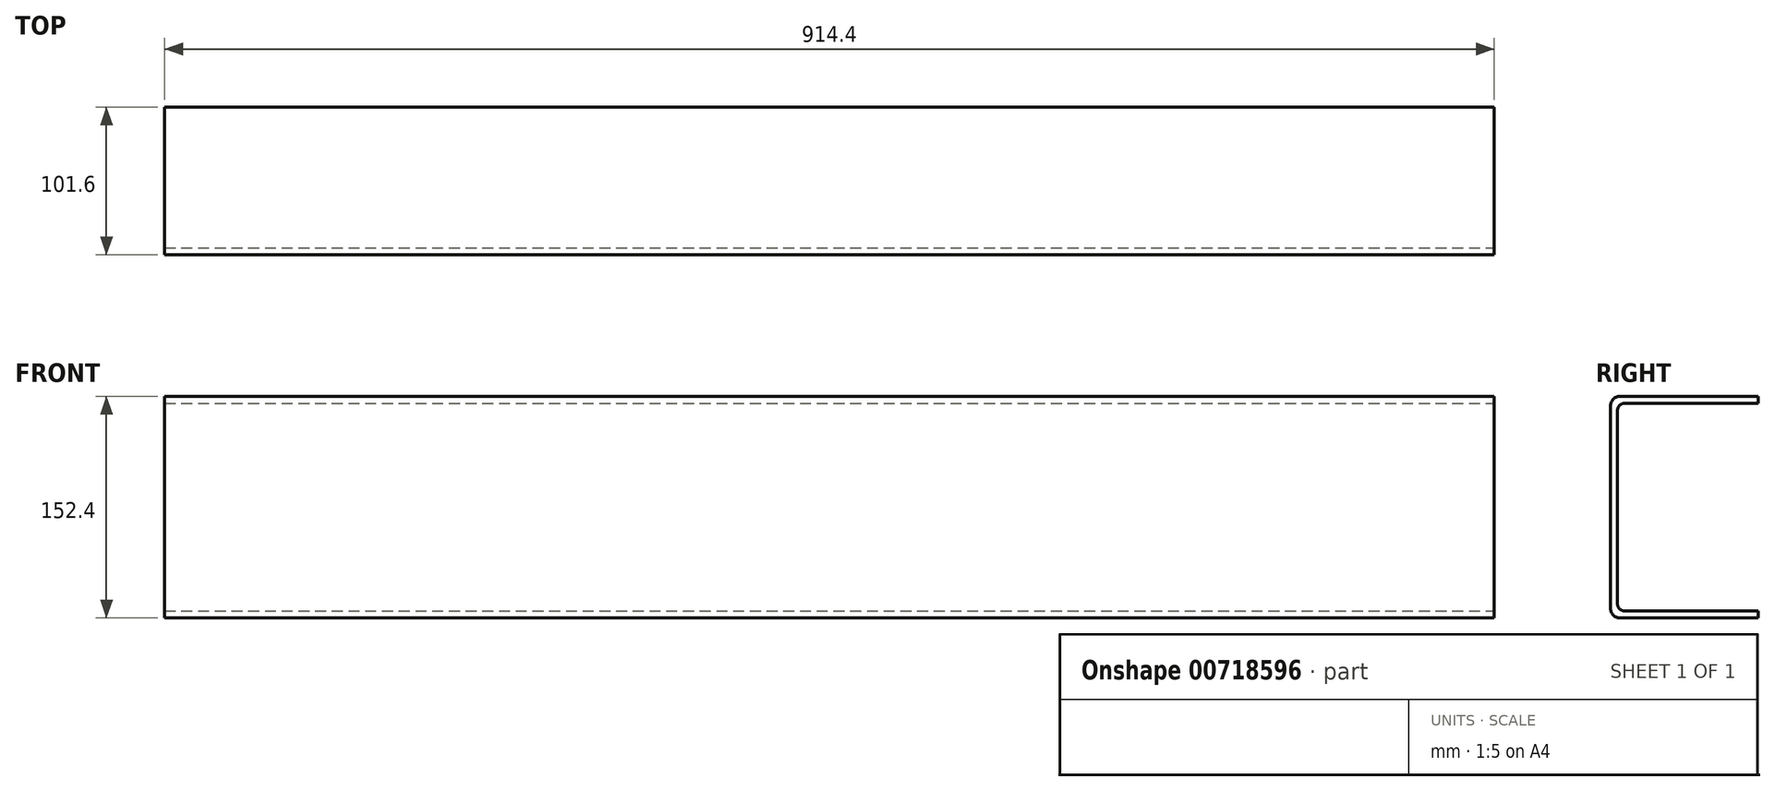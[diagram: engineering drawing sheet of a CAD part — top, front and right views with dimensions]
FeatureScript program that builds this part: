
annotation { "Feature Type Name" : "Feature", "Feature Type Description" : "" }
export const myFeature = defineFeature(function(context is Context, id is Id, definition is map)
    precondition{}
    {
        {
            var Q0;
            Q0=qCreatedBy(makeId("Right.planeOp"),FACE);
            var sketch = newSketch(context, id + "F0", { "sketchPlane" : qUnion([Q0])});
            skLineSegment(sketch, "E0", {"start": v(101.6, 76.2) * mm, "end": v(6.35, 76.2) * mm});
            skLineSegment(sketch, "E1", {"start": v(0, 69.85) * mm, "end": v(0, 0) * mm});
            skLineSegment(sketch, "E2", {"start": v(-101.6, 0) * mm, "end": v(84.67, 0) * mm, "construction": true});
            skLineSegment(sketch, "E3.MirrorCS", {"start": v(101.6, -76.2) * mm, "end": v(6.35, -76.2) * mm});
            skLineSegment(sketch, "E4.MirrorCS", {"start": v(0, -69.85) * mm, "end": v(0, 0) * mm});
            skLineSegment(sketch, "E5.0", {"start": v(101.6, -71.44) * mm, "end": v(9.53, -71.44) * mm});
            skLineSegment(sketch, "E5.1", {"start": v(4.76, -66.67) * mm, "end": v(4.76, 0) * mm});
            skLineSegment(sketch, "E5.2", {"start": v(4.76, 66.67) * mm, "end": v(4.76, 0) * mm});
            skLineSegment(sketch, "E5.3", {"start": v(101.6, 71.44) * mm, "end": v(9.52, 71.44) * mm});
            skLineSegment(sketch, "E6", {"start": v(101.6, 76.2) * mm, "end": v(101.6, 71.44) * mm});
            skLineSegment(sketch, "E7", {"start": v(101.6, -76.2) * mm, "end": v(101.6, -71.44) * mm});
            skPoint(sketch, "E8.visualSharp", {"position": v(0, 76.2) * mm});
            skArc(sketch, "E8.filletArc", {"start": v(6.35, 76.2) * mm, "mid": v(1.86, 74.34) * mm, "end": v(0, 69.85) * mm});
            skPoint(sketch, "E9.visualSharp", {"position": v(4.76, 71.44) * mm});
            skArc(sketch, "E9.filletArc", {"start": v(9.52, 71.44) * mm, "mid": v(6.16, 70.04) * mm, "end": v(4.76, 66.67) * mm});
            skPoint(sketch, "E10.visualSharp", {"position": v(0, -76.2) * mm});
            skArc(sketch, "E10.filletArc", {"start": v(0, -69.85) * mm, "mid": v(1.86, -74.34) * mm, "end": v(6.35, -76.2) * mm});
            skArc(sketch, "E11.filletArc", {"start": v(4.76, -66.67) * mm, "mid": v(6.16, -70.04) * mm, "end": v(9.53, -71.44) * mm});
            skSolve(sketch);
        }
        {
            var Q0;
            Q0=makeQuery(id+"F0.imprint","IMPRINT",FACE,{"disambiguationData":[TD([[makeQuery(id+"F0.imprint","IMPRINT",EDGE,{"derivedFrom":sQuery(id+"F0.wireOp",EDGE,"E0")}),1.0]])]});
            extrude(context, id + "F1", {"entities" : qUnion([Q0]), "oppositeDirection" : true, "depth" : 457.2 * mm, "offsetDistance" : 25.4 * mm, "hasSecondDirection" : true, "secondDirectionOppositeDirection" : false, "secondDirectionDepth" : 457.2 * mm});
        }
        {
            var Q0;
            Q0=makeQuery(id+"F1.opExtrude","CAP_FACE",FACE,{"disambiguationData":[OSD([sQuery(id+"F0.wireOp",EDGE,"E0"),sQuery(id+"F0.wireOp",EDGE,"E1"),sQuery(id+"F0.wireOp",EDGE,"E3.MirrorCS"),sQuery(id+"F0.wireOp",EDGE,"E4.MirrorCS"),sQuery(id+"F0.wireOp",EDGE,"E5.0"),sQuery(id+"F0.wireOp",EDGE,"E5.1"),sQuery(id+"F0.wireOp",EDGE,"E5.2"),sQuery(id+"F0.wireOp",EDGE,"E5.3"),sQuery(id+"F0.wireOp",EDGE,"E6"),sQuery(id+"F0.wireOp",EDGE,"E7"),sQuery(id+"F0.wireOp",EDGE,"E8.filletArc"),sQuery(id+"F0.wireOp",EDGE,"E9.filletArc"),sQuery(id+"F0.wireOp",EDGE,"E10.filletArc"),sQuery(id+"F0.wireOp",EDGE,"E11.filletArc")])],"isStart":true});
            var Q1;
            Q1=makeQuery(id+"F1.opExtrude","CAP_FACE",FACE,{"disambiguationData":[OSD([sQuery(id+"F0.wireOp",EDGE,"E0"),sQuery(id+"F0.wireOp",EDGE,"E1"),sQuery(id+"F0.wireOp",EDGE,"E3.MirrorCS"),sQuery(id+"F0.wireOp",EDGE,"E4.MirrorCS"),sQuery(id+"F0.wireOp",EDGE,"E5.0"),sQuery(id+"F0.wireOp",EDGE,"E5.1"),sQuery(id+"F0.wireOp",EDGE,"E5.2"),sQuery(id+"F0.wireOp",EDGE,"E5.3"),sQuery(id+"F0.wireOp",EDGE,"E6"),sQuery(id+"F0.wireOp",EDGE,"E7"),sQuery(id+"F0.wireOp",EDGE,"E8.filletArc"),sQuery(id+"F0.wireOp",EDGE,"E9.filletArc"),sQuery(id+"F0.wireOp",EDGE,"E10.filletArc"),sQuery(id+"F0.wireOp",EDGE,"E11.filletArc")])],"isStart":false});
            cPlane(context, id + "F2", {"entities" : qUnion([Q0, Q1]), "cplaneType" : CPlaneType.MID_PLANE, "offset" : 25.4 * mm, "width" : 152.4 * mm, "height" : 152.4 * mm});
        }
    });
